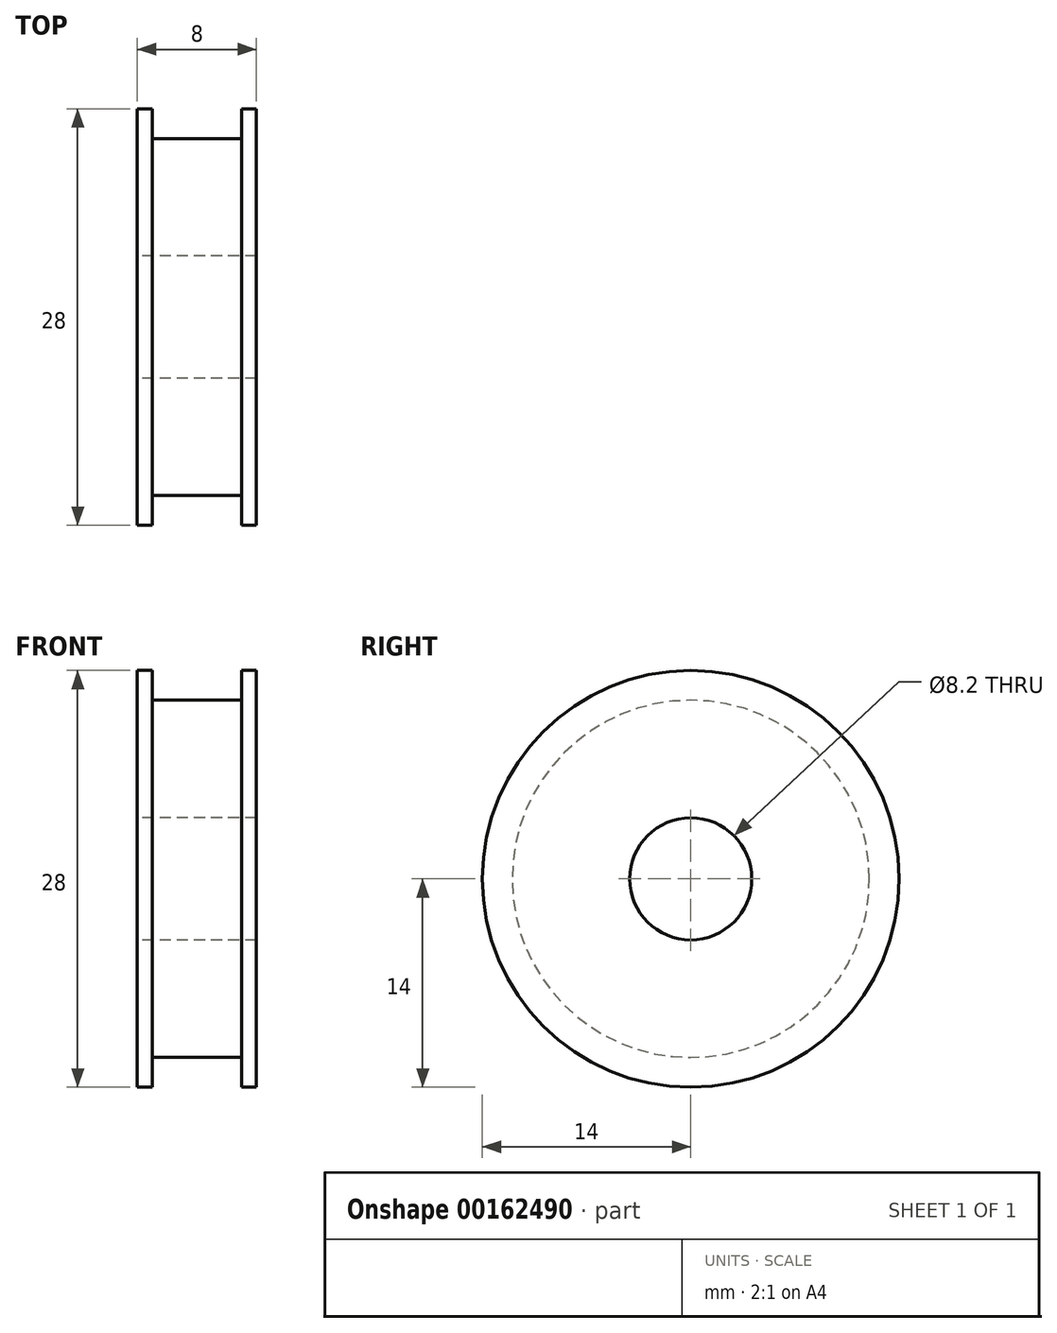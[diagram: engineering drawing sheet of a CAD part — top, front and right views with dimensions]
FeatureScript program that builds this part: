
annotation { "Feature Type Name" : "Feature", "Feature Type Description" : "" }
export const myFeature = defineFeature(function(context is Context, id is Id, definition is map)
    precondition{}
    {
        {
            var Q0;
            Q0=qCreatedBy(makeId("Top.planeOp"),FACE);
            var sketch = newSketch(context, id + "F0", { "sketchPlane" : qUnion([Q0])});
            skLineSegment(sketch, "E0", {"start": v(0, 4.1) * mm, "end": v(4, 4.1) * mm});
            skLineSegment(sketch, "E1", {"start": v(4, 4.1) * mm, "end": v(4, 14) * mm});
            skLineSegment(sketch, "E2", {"start": v(4, 14) * mm, "end": v(3, 14) * mm});
            skLineSegment(sketch, "E3", {"start": v(3, 14) * mm, "end": v(3, 12) * mm});
            skLineSegment(sketch, "E4", {"start": v(3, 12) * mm, "end": v(0, 12) * mm});
            skLineSegment(sketch, "E5", {"start": v(0, 0) * mm, "end": v(0, 14.26) * mm, "construction": true});
            skLineSegment(sketch, "E6.MirrorCS", {"start": v(-3, 12) * mm, "end": v(0, 12) * mm});
            skLineSegment(sketch, "E7.MirrorCS", {"start": v(-3, 14) * mm, "end": v(-3, 12) * mm});
            skLineSegment(sketch, "E8.MirrorCS", {"start": v(-4, 14) * mm, "end": v(-3, 14) * mm});
            skLineSegment(sketch, "E9.MirrorCS", {"start": v(-4, 4.1) * mm, "end": v(-4, 14) * mm});
            skLineSegment(sketch, "E10.MirrorCS", {"start": v(0, 4.1) * mm, "end": v(-4, 4.1) * mm});
            skLineSegment(sketch, "E11", {"start": v(0, 0) * mm, "end": v(7.98, 0) * mm, "construction": true});
            skSolve(sketch);
        }
        {
            var Q0;
            Q0=qSketchRegion(id+"F0",true);
            var Q1;
            Q1=sQuery(id+"F0.wireOp",EDGE,"E11");
            revolve(context, id + "F1", {"entities" : qUnion([Q0]), "axis" : qUnion([Q1]), "revolveType" : RevolveType.FULL});
        }
    });
